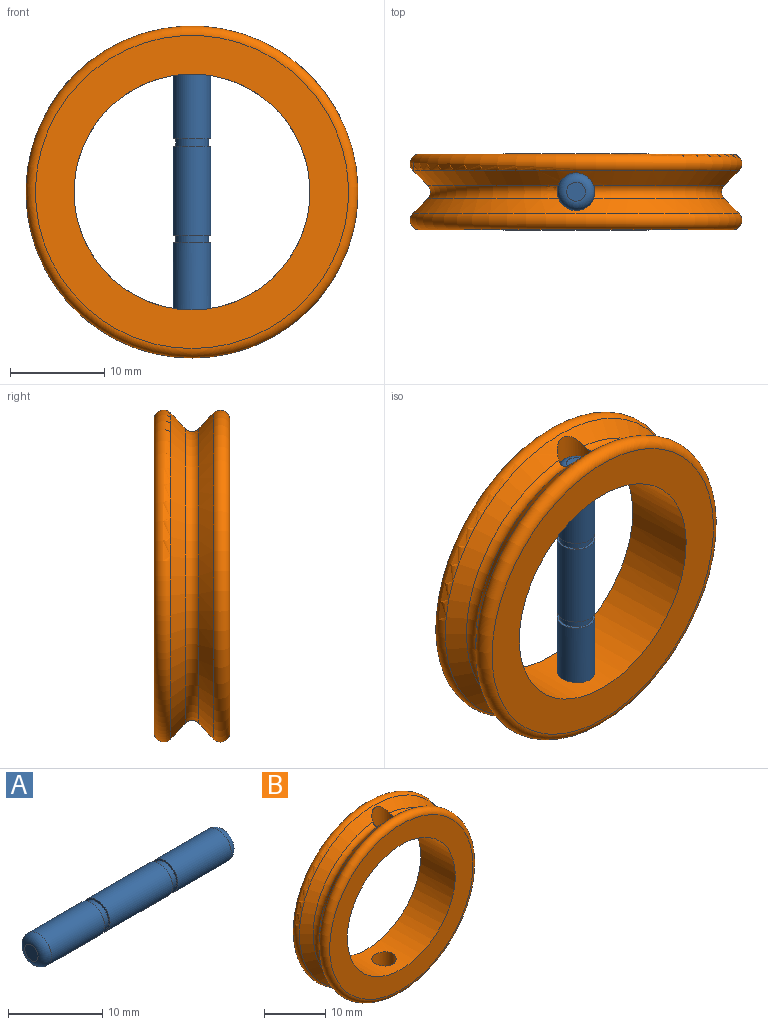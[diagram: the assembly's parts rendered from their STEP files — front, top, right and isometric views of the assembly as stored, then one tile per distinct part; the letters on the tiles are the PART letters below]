
ASSEMBLY  parts=2 mates=1
PART A: 13 faces, bbox 29x4.3x4.3 mm
  f0: cylinder r=2mm len=8mm, axis (1,0,0), area 100.5mm2, adj f6,f11
  f1: cylinder r=2mm len=8mm, axis (1,0,0), area 100.5mm2, adj f7,f12
  f2: plane 4x4mm, normal (1,0,0), area 2.9mm2, adj f3,f8
  f3: cylinder r=2mm len=9.4mm, axis (1,0,0), area 118.1mm2, adj f2,f4
  f4: plane 4x4mm, normal (-1,0,0), area 2.9mm2, adj f3,f5
  f5: cylinder r=1.75mm len=3.5mm, axis (1,0,0), area 8.8mm2, adj f4,f6
  f6: plane 4x4mm, normal (1,0,0), area 2.9mm2, adj f0,f5
  f7: plane 4x4mm, normal (-1,0,0), area 2.9mm2, adj f1,f8
  f8: cylinder r=1.75mm len=3.5mm, axis (1,0,0), area 8.8mm2, adj f2,f7
  f9: plane 2x2mm, normal (1,0,0), area 3.1mm2, adj f12
  f10: plane 2x2mm, normal (-1,0,0), area 3.1mm2, adj f11
  f11: torus R=1mm, axis (-1,0,0), area 16.2mm2, adj f0,f10
  f12: torus R=1mm, axis (1,0,0), area 16.2mm2, adj f1,f9
PART B: 11 faces, bbox 38.1x8x38.1 mm
  f0: cone r=15mm half-angle=45deg, axis (0,-1,0), area 222.6mm2, adj f2,f3,f8,f9,f10
  f1: cone r=15mm half-angle=45deg, axis (0,1,0), area 222.5mm2, adj f2,f3,f7,f9,f10
  f2: torus R=16.41mm, axis (0,-1,0), area 70.4mm2, adj f0,f1,f9,f10
  f3: torus R=16.41mm, axis (0,-1,0), area 70.4mm2, adj f0,f1,f9,f10
  f4: cylinder r=12.5mm len=25mm, axis (0,-1,0), area 603.1mm2, adj f5,f6,f9,f10
  f5: plane 33.17x33.17mm, normal (0,-1,0), area 373.3mm2, adj f4,f8
  f6: plane 33.17x33.17mm, normal (0,1,0), area 373.3mm2, adj f4,f7
  f7: torus R=16.59mm, axis (0,1,0), area 256.3mm2, adj f1,f6
  f8: torus R=16.59mm, axis (0,-1,0), area 256.3mm2, adj f0,f5
  f9: cylinder r=2mm len=4.66mm, axis (0,0,1), area 48.1mm2, adj f0,f1,f2,f3,f4
  f10: cylinder r=2mm len=4.66mm, axis (0,0,-1), area 48.1mm2, adj f0,f1,f2,f3,f4
PLACE A rot(axis=(0,-1,0),90deg) t=(-1.58,15.21,-22.05)mm
PLACE B t=(-1.58,15.21,-4.69)mm
MATE cylindrical A.f0 <-> B.f9  axis (0,0,-1) through (-1.58,15.21,8.95)mm
